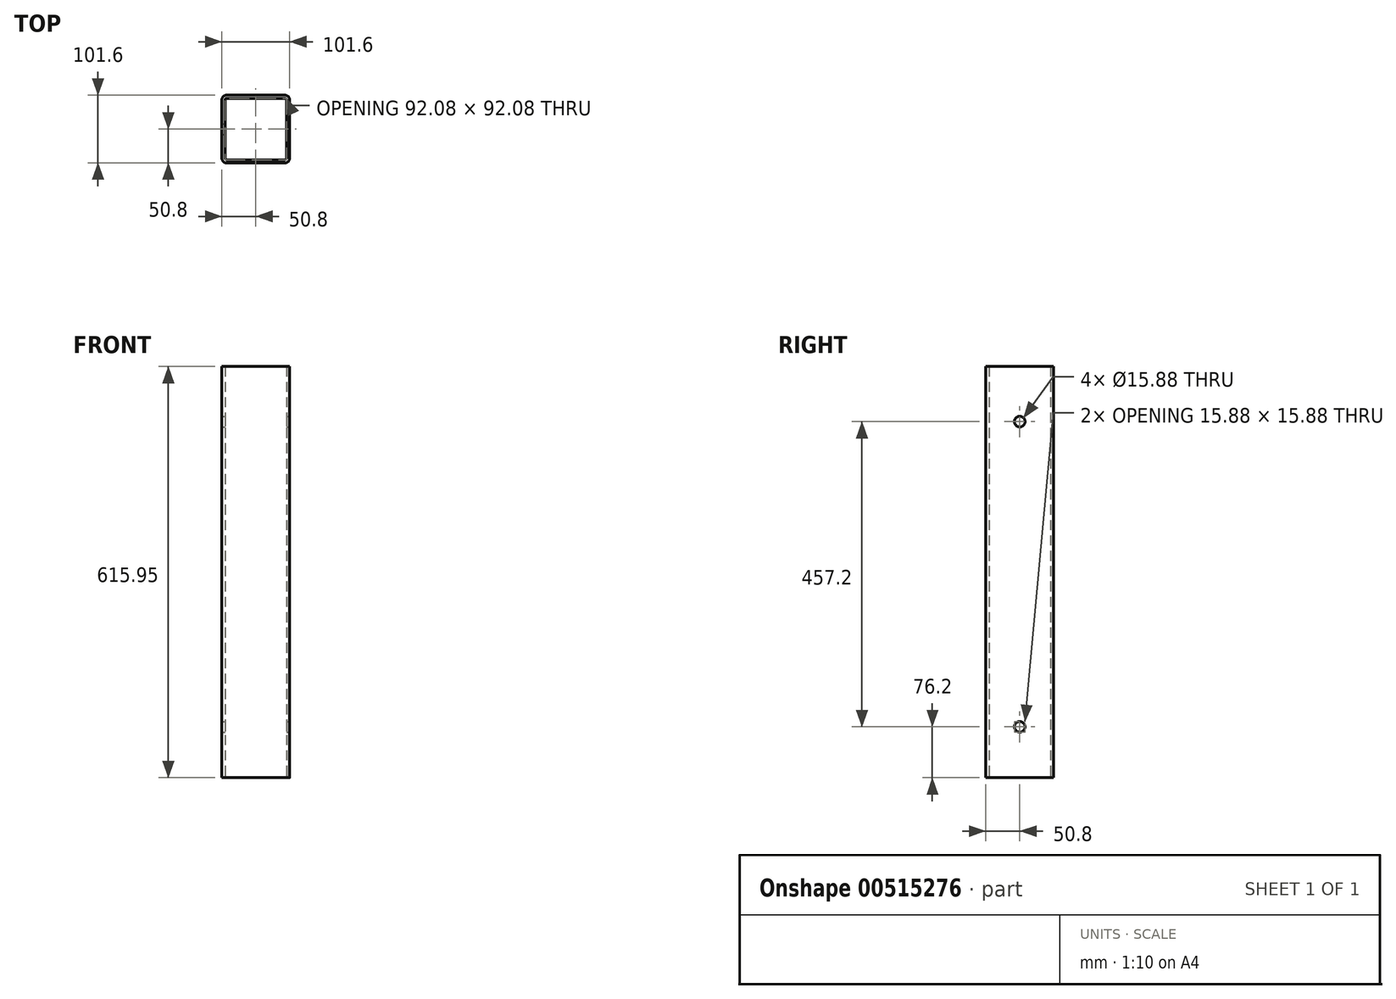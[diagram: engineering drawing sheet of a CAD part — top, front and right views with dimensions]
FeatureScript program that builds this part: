
annotation { "Feature Type Name" : "Feature", "Feature Type Description" : "" }
export const myFeature = defineFeature(function(context is Context, id is Id, definition is map)
    precondition{}
    {
        {
            var Q0;
            Q0=qCreatedBy(makeId("Top.planeOp"),FACE);
            var sketch = newSketch(context, id + "F0", { "sketchPlane" : qUnion([Q0])});
            skLineSegment(sketch, "E0.bottom", {"start": v(-43.66, 50.8) * mm, "end": v(43.66, 50.8) * mm});
            skLineSegment(sketch, "E0.top", {"start": v(-43.66, -50.8) * mm, "end": v(43.66, -50.8) * mm});
            skLineSegment(sketch, "E0.left", {"start": v(-50.8, 43.66) * mm, "end": v(-50.8, -43.66) * mm});
            skLineSegment(sketch, "E0.right", {"start": v(50.8, 43.66) * mm, "end": v(50.8, -43.66) * mm});
            skPoint(sketch, "E1.visualSharp", {"position": v(50.8, 50.8) * mm});
            skArc(sketch, "E1.filletArc", {"start": v(50.8, 43.66) * mm, "mid": v(48.7, 48.7) * mm, "end": v(43.66, 50.8) * mm});
            skPoint(sketch, "E2.visualSharp", {"position": v(-50.8, 50.8) * mm});
            skArc(sketch, "E2.filletArc", {"start": v(-43.66, 50.8) * mm, "mid": v(-48.7, 48.7) * mm, "end": v(-50.8, 43.66) * mm});
            skPoint(sketch, "E3.visualSharp", {"position": v(-50.8, -50.8) * mm});
            skArc(sketch, "E3.filletArc", {"start": v(-50.8, -43.66) * mm, "mid": v(-48.7, -48.7) * mm, "end": v(-43.66, -50.8) * mm});
            skPoint(sketch, "E4.visualSharp", {"position": v(50.8, -50.8) * mm});
            skArc(sketch, "E4.filletArc", {"start": v(43.66, -50.8) * mm, "mid": v(48.7, -48.7) * mm, "end": v(50.8, -43.66) * mm});
            skLineSegment(sketch, "E5.bottom", {"start": v(-43.66, -46.04) * mm, "end": v(43.66, -46.04) * mm});
            skLineSegment(sketch, "E5.top", {"start": v(-43.66, 46.04) * mm, "end": v(43.66, 46.04) * mm});
            skLineSegment(sketch, "E5.left", {"start": v(-46.04, -43.66) * mm, "end": v(-46.04, 43.66) * mm});
            skLineSegment(sketch, "E5.right", {"start": v(46.04, -43.66) * mm, "end": v(46.04, 43.66) * mm});
            skPoint(sketch, "E5.middle", {"position": v(0, 0) * mm});
            skPoint(sketch, "E6.visualSharp", {"position": v(46.04, 46.04) * mm});
            skArc(sketch, "E6.filletArc", {"start": v(46.04, 43.66) * mm, "mid": v(45.34, 45.34) * mm, "end": v(43.66, 46.04) * mm});
            skPoint(sketch, "E7.visualSharp", {"position": v(-46.04, 46.04) * mm});
            skArc(sketch, "E7.filletArc", {"start": v(-43.66, 46.04) * mm, "mid": v(-45.34, 45.34) * mm, "end": v(-46.04, 43.66) * mm});
            skPoint(sketch, "E8.visualSharp", {"position": v(-46.04, -46.04) * mm});
            skArc(sketch, "E8.filletArc", {"start": v(-46.04, -43.66) * mm, "mid": v(-45.34, -45.34) * mm, "end": v(-43.66, -46.04) * mm});
            skPoint(sketch, "E9.visualSharp", {"position": v(46.04, -46.04) * mm});
            skArc(sketch, "E9.filletArc", {"start": v(43.66, -46.04) * mm, "mid": v(45.34, -45.34) * mm, "end": v(46.04, -43.66) * mm});
            skLineSegment(sketch, "E10", {"start": v(0, 50.8) * mm, "end": v(0, -50.8) * mm, "construction": true});
            skLineSegment(sketch, "E11", {"start": v(-50.8, 0) * mm, "end": v(50.8, 0) * mm, "construction": true});
            skSolve(sketch);
        }
        {
            var Q0;
            Q0=qSketchRegion(id+"F0",true);
            extrude(context, id + "F1", {"entities" : qUnion([Q0]), "depth" : 615.95 * mm, "offsetDistance" : 25.4 * mm});
        }
        {
            var Q0;
            Q0=makeQuery(id+"F1.opExtrude","SWEPT_FACE",FACE,{"disambiguationData":[OSD([sQuery(id+"F0.wireOp",EDGE,"E0.right")])]});
            var sketch = newSketch(context, id + "F2", { "sketchPlane" : qUnion([Q0])});
            skCircle(sketch, "E12", {"center": v(0, 76.2) * mm, "radius": 7.94 * mm});
            skCircle(sketch, "E13", {"center": v(0, 533.4) * mm, "radius": 7.94 * mm});
            skSolve(sketch);
        }
        {
            var Q0;
            Q0=qSketchRegion(id+"F2",true);
            extrude(context, id + "F3", {"entities" : qUnion([Q0]), "operationType" : NewBodyOperationType.REMOVE, "endBound" : BoundingType.THROUGH_ALL, "oppositeDirection" : true, "depth" : 25.4 * mm, "offsetDistance" : 25.4 * mm});
        }
    });
